# Revit family: Window-Exterior-Simpson-French-Transom
name_source: partatom
category: Windows
revit_build: Autodesk Revit Architecture 2012 (Build: 20120126_0600(x64)
units: mm (PartAtom-declared; Revit-internal decimal feet)

## types (41) — shared parameters
Assembly Code = B2020100
Default Sill Height = 70"
Glass = Glass - Simpson Doors - Clear
Glass Options = http://simpsondoor.com
Glass Thickness = 3/4"
Manufacturer = Simpson Door Company
Notes = Dozens of glass textures and colors are available. For a list of standard options visit the Simpson web site or submit a custom glass request: http://simpsondoor.com
Ovolo Construction = Yes
Panel = Wood - Simpson Doors - Douglas Fir
Panel Thickness = 1 3/4"
Product Documentation Link = http://www.simpsondoor.com
Product Page URL = http://www.simpsondoor.com
URL = http://www.simpsondoor.com
UltraBlock Note = This Door Comes with The Option of UltraBlock Technology. It is Turn On as a Default
UltraBlock Option = Yes
Wall Closure = By host
WaterBarrier Note = This Door Comes with The Option of WaterBarrier with UltraBlock Technology. It is Turn Off as a Default
WaterBarrier with UltraBlock Technology = No
Wood Species = http://simpsondoor.com
Wood Species Note = Available in Any Wood Species

## per-type parameters (varying)
| type | Bottom Rail Height | Description | Height | Model | Number of Horizontal Muntins | Number of Vertical Muntins | Panel Stile Width | Top Rail Height | Width |
| 7751 Transom 12.25x12 | 2 13/32" | Exterior French - One Lite - Transom | 12" | 7751 | 0 | 0 | 1 13/32" | 2 13/32" | 12 1/4" |
| 7751 Transom 22.5x12 | 2 13/32" | Exterior French - One Lite - Transom | 12" | 7751 | 0 | 0 | 5" | 2 13/32" | 22 1/2" |
| 7751 Transom 36x12 | 2 13/32" | Exterior French - One Lite - Transom | 12" | 7751 | 0 | 0 | 5" | 2 13/32" | 36" |
| 7751 Transom 72x12 | 2 13/32" | Exterior French - One Lite - Transom | 12" | 7751 | 0 | 0 | 5" | 2 13/32" | 72" |
| 7751 Transom 17x14 | 2 13/32" | Exterior French - One Lite - Transom | 14" | 7751 | 0 | 0 | 3 13/32" | 2 13/32" | 17" |
| 7751 Transom 72.75x14 | 2 13/32" | Exterior French - One Lite - Transom | 14" | 7751 | 0 | 0 | 5" | 2 13/32" | 72 3/4" |
| 7751 Transom 41x16 | 2 13/32" | Exterior French - One Lite - Transom | 16" | 7751 | 0 | 0 | 5" | 2 13/32" | 41" |
| 7751 Transom 36x17 | 2 13/32" | Exterior French - One Lite - Transom | 17 13/16" | 7751 | 0 | 0 | 4" | 2 13/32" | 36" |
| 7751 Transom 60x18 | 2 13/32" | Exterior French - One Lite - Transom | 18" | 7751 | 0 | 0 | 5" | 2 13/32" | 60" |
| 7751 Transom 36x20 | 2 13/32" | Exterior French - One Lite - Transom | 20" | 7751 | 0 | 0 | 2 13/32" | 2 13/32" | 36" |
| 7751 Transom 20x24 | 2 13/32" | Exterior French - One Lite - Transom | 24" | 7751 | 0 | 0 | 2 13/32" | 2 13/32" | 20" |
| 7751 Transom 36x24 | 2 13/32" | Exterior French - One Lite - Transom | 24" | 7751 | 0 | 0 | 4" | 2 13/32" | 36" |
| 7751 Transom 73.25x24 | 2 13/32" | Exterior French - One Lite - Transom | 24" | 7751 | 0 | 0 | 4" | 2 13/32" | 73 1/4" |
| 7755 Transom 63x10.5 | 2 13/32" | Exterior French - Five Lite - Transom | 10 1/2" | 7755 | 0 | 4 | 2 13/32" | 2 13/32" | 63" |
| 7755 Transom 24.1875x12 | 2 13/32" | Exterior French - Two Lite - Transom | 12" | 7755 | 0 | 1 | 2 13/32" | 2 13/32" | 24 3/16" |
| 7755 Transom 61x12 | 1 13/32" | Exterior French - Five Lite - Transom | 12" | 7755 | 0 | 4 | 5" | 1 13/32" | 61" |
| 7755 Transom 62x12 | 2 13/32" | Exterior French - Five Lite - Transom | 12" | 7755 | 0 | 4 | 5" | 2 13/32" | 72" |
| 7755 Transom 62.25x12 | 2 13/32" | Exterior French - Seven Lite - Transom | 12" | 7755 | 0 | 6 | 1 13/32" | 2 13/32" | 62 1/4" |
| 7755 Transom 66x12 | 2 13/32" | Exterior French - Five Lite - Transom | 12" | 7755 | 0 | 4 | 2 9/32" | 2 13/32" | 66 3/16" |
| 7755 Transom 71x12 | 2 13/32" | Exterior French - Five Lite - Transom | 12" | 7755 | 0 | 4 | 5" | 2 13/32" | 71" |
| 7755 Transom 87.25x12 | 2 13/32" | Exterior French - Nine Lite - Transom | 12" | 7755 | 0 | 8 | 2 13/32" | 2 13/32" | 87 1/4" |
| 7755 Transom 36x14 | 2 13/32" | Exterior French - Five Lite - Transom | 14" | 7755 | 0 | 4 | 5" | 2 13/32" | 36" |
| 7755 Transom49.25x14 | 2 13/32" | Exterior French - Five Lite - Transom | 14" | 7755 | 0 | 4 | 4 1/8" | 2 13/32" | 49 1/4" |
| 7755 Transom 60.75x14 | 2 13/32" | Exterior French - Five Lite - Transom | 14" | 7755 | 0 | 4 | 5" | 2 13/32" | 60 3/4" |
| 7755 Transom 62x14 | 2 13/32" | Exterior French - Five Lite - Transom | 14" | 7755 | 0 | 4 | 5" | 2 13/32" | 62" |
| 7755 Transom 64.75x14 | 2 13/32" | Exterior French - Five Lite - Transom | 14" | 7755 | 0 | 4 | 5" | 2 13/32" | 64 3/4" |
| 7755 Transom 66x14 | 1 13/32" | Exterior French - Five Lite - Transom | 14" | 7755 | 0 | 4 | 1 13/32" | 1 13/32" | 66" |
| 7755 Transom 66.5x14 | 2 13/32" | Exterior French - Five Lite - Transom | 14" | 7755 | 0 | 4 | 5" | 2 13/32" | 66 1/2" |
| 7755 Transom 72x14 | 2 13/32" | Exterior French - Five Lite - Transom | 14" | 7755 | 0 | 4 | 5" | 2 13/32" | 72" |
| 7755 Transom 75x14 | 2 13/32" | Exterior French - Five Lite - Transom | 14" | 7755 | 0 | 4 | 5" | 2 13/32" | 75" |
| 7755 Transom 81x14 | 2 13/32" | Exterior French - Five Lite - Transom | 14" | 7755 | 0 | 4 | 2 13/32" | 2 13/32" | 81" |
| 7755 Transom 16x16 | 2 13/32" | Exterior French - Two Lite - Transom | 16" | 7755 | 0 | 1 | 2 13/32" | 2 13/32" | 16" |
| 7755 Transom 42.25x16 | 2 13/32" | Exterior French - Five Lite - Transom | 16" | 7755 | 0 | 4 | 2 13/32" | 2 13/32" | 42 1/4" |
| 7755 Transom 93.25x16 | 2 13/32" | Exterior French - Five Lite - Transom | 16" | 7755 | 0 | 4 | 5" | 2 13/32" | 93 1/4" |
| 7755 Transom 32x16.5 | 2 13/32" | Exterior French - Three Lite - Transom | 16 1/2" | 7755 | 0 | 2 | 2 13/32" | 2 13/32" | 32" |
| 7755 Transom 36x16.5 | 2 13/32" | Exterior French - Three Lite - Transom | 16 1/2" | 7755 | 0 | 2 | 2 13/32" | 2 13/32" | 36" |
| 7755 Transom 20.1875x18 | 2 13/32" | Exterior French - Four Lite - Transom | 18" | 7755 | 1 | 1 | 2 13/32" | 2 13/32" | 20 3/16" |
| 7755 Transom 36x18 | 2 13/32" | Exterior French - Five Lite - Transom | 18" | 7755 | 0 | 4 | 5" | 2 13/32" | 36" |
| 7755 Transom 36.1875x18 | 2 13/32" | Exterior French - Eight Lite - Transom | 18" | 7755 | 1 | 3 | 2 13/32" | 2 13/32" | 36 3/16" |
| 7755 Transom 63.75x23.5 | 2 13/32" | Exterior French - Ten Lite - Transom | 23 1/2" | 7755 | 1 | 4 | 4" | 2 13/32" | 63 3/4" |
| 7755 Transom 36.1875x24 | 2 13/32" | Exterior French - Eight Lite - Transom | 24" | 7755 | 1 | 3 | 5 3/32" | 2 13/32" | 36 3/16" |

## geometry (parser evidence)
native form markers: Blend x30, Sweep x4
no freeform markers — native parametric forms only
